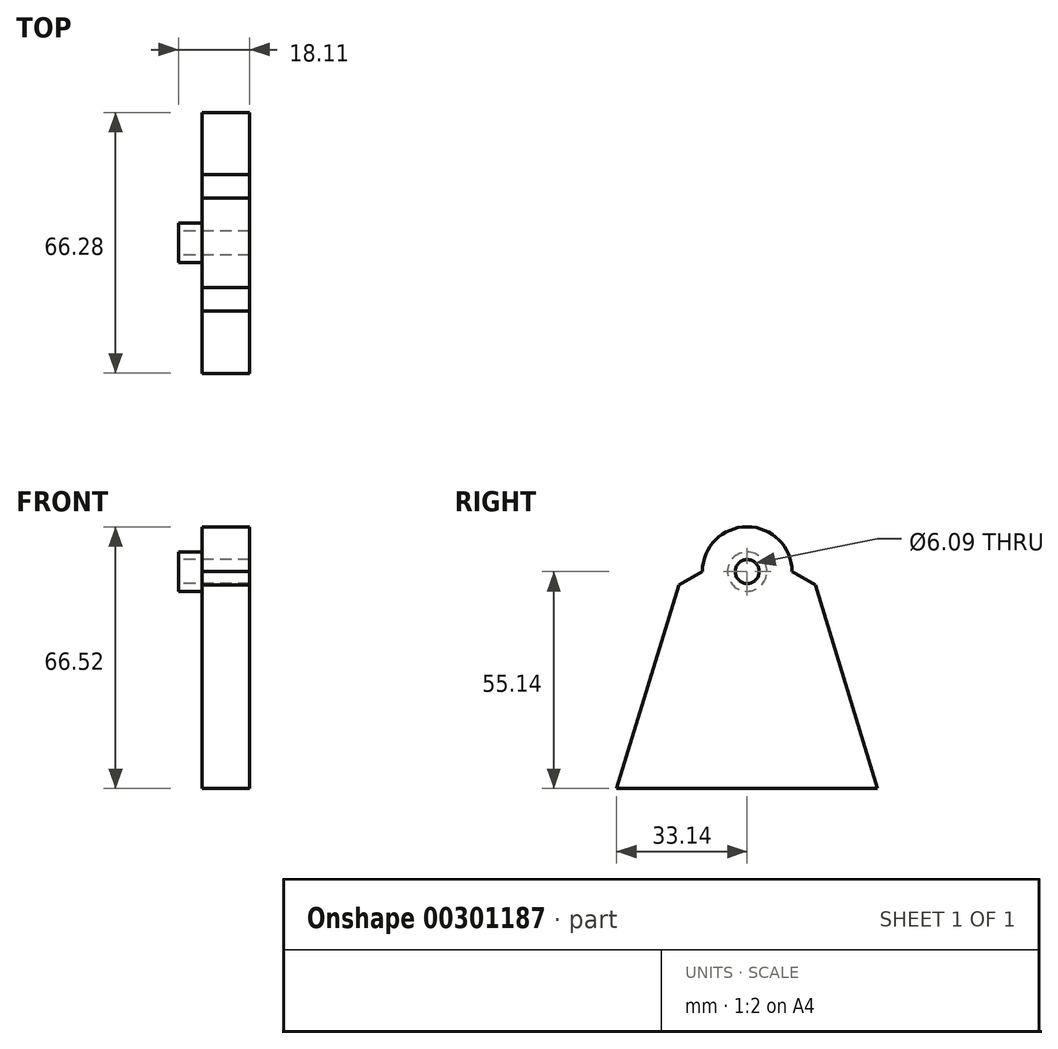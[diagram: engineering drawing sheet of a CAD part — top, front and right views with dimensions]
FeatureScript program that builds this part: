
annotation { "Feature Type Name" : "Feature", "Feature Type Description" : "" }
export const myFeature = defineFeature(function(context is Context, id is Id, definition is map)
    precondition{}
    {
        {
            var Q0;
            Q0=qCreatedBy(makeId("Right.planeOp"),FACE);
            var sketch = newSketch(context, id + "F0", { "sketchPlane" : qUnion([Q0])});
            skCircle(sketch, "E0", {"center": v(0, 0) * mm, "radius": 5 * mm});
            skSolve(sketch);
        }
        {
            var Q0;
            Q0 = qSketchRegion(id + "F0", true);
            extrude(context, id + "F1", {"entities" : qUnion([Q0]), "oppositeDirection" : true, "depth" : (12.07 / 2) * mm});
        }
        {
            var Q0;
            Q0=makeQuery(id+"F1.opExtrude","CAP_FACE",FACE,{"disambiguationData":[OSD([sQuery(id+"F0.wireOp",EDGE,"E0")])],"isStart":true});
            var sketch = newSketch(context, id + "F2", { "sketchPlane" : qUnion([Q0])});
            skCircle(sketch, "E1", {"center": v(0, 0) * mm, "radius": 11.38 * mm});
            skSolve(sketch);
        }
        {
            var Q0;
            Q0 = qSketchRegion(id + "F2", true);
            extrude(context, id + "F3", {"entities" : qUnion([Q0]), "operationType" : NewBodyOperationType.ADD, "depth" : 12.07 * mm});
        }
        {
            var Q0;
            Q0=makeQuery(id+"F3.opExtrude","CAP_FACE",FACE,{"disambiguationData":[OSD([sQuery(id+"F2.wireOp",EDGE,"E1")])],"isStart":false});
            var sketch = newSketch(context, id + "F4", { "sketchPlane" : qUnion([Q0])});
            skLineSegment(sketch, "E2", {"start": v(-11.38, 0) * mm, "end": v(-17.28, -3.4) * mm});
            skLineSegment(sketch, "E3", {"start": v(-17.28, -3.4) * mm, "end": v(-33.14, -55.14) * mm});
            skLineSegment(sketch, "E4", {"start": v(-33.14, -55.14) * mm, "end": v(0, -55.14) * mm});
            skLineSegment(sketch, "E5.MirrorCS", {"start": v(11.38, 0) * mm, "end": v(17.28, -3.4) * mm});
            skLineSegment(sketch, "E6.MirrorCS", {"start": v(17.28, -3.4) * mm, "end": v(33.14, -55.14) * mm});
            skLineSegment(sketch, "E7.MirrorCS", {"start": v(33.14, -55.14) * mm, "end": v(0, -55.14) * mm});
            skArc(sketch, "E8", {"start": v(-11.38, 0) * mm, "mid": v(0, -11.38) * mm, "end": v(11.38, 0) * mm});
            skSolve(sketch);
        }
        {
            var Q0;
            Q0 = qSketchRegion(id + "F4", true);
            extrude(context, id + "F5", {"entities" : qUnion([Q0]), "operationType" : NewBodyOperationType.ADD, "oppositeDirection" : true, "depth" : 12.07 * mm});
        }
        {
            var Q0;
            Q0=makeQuery(id+"F1.opExtrude","CAP_FACE",FACE,{"disambiguationData":[OSD([sQuery(id+"F0.wireOp",EDGE,"E0")])],"isStart":false});
            var sketch = newSketch(context, id + "F6", { "sketchPlane" : qUnion([Q0])});
            skCircle(sketch, "E9", {"center": v(0, 0) * mm, "radius": 3.05 * mm});
            skSolve(sketch);
        }
        {
            var Q0;
            Q0 = qSketchRegion(id + "F6", true);
            extrude(context, id + "F7", {"entities" : qUnion([Q0]), "operationType" : NewBodyOperationType.REMOVE, "oppositeDirection" : true, "depth" : 25 * mm});
        }
    });
